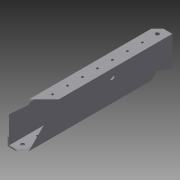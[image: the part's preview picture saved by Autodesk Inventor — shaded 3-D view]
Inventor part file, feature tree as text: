
AUTODESK INVENTOR PART (.ipt)
format: ipt  version: 2015 SP1 (Build 190203100, 203)  size: 138,752 bytes
history: native  units: in
note: dims shown in document units (in); Inventor stores cm internally (conversion verified against a paired STEP export)
features: sketch x4, projected_geometry x3, extrude x2, hole x2, pattern_linear x1
ambient origin geometry x8: Origin, YZ Plane, XZ Plane, XY Plane, X Axis, Y Axis, Z Axis, Center Point
bodies: Solid1 (feature_tree)
feature tree (12):
  extrude  "Extrusion1"  Depth=2.0in
  hole  "Hole1"  [1 undecoded]
  pattern_linear  "Rectangular Pattern1"  Spacing1=10.0in  [1 undecoded]
  extrude  "Extrusion2"  Depth=1.0in
  hole  "Hole2"  [1 undecoded]
  sketch  "Sketch1"  dims[d0=1.0in d1=2.0in]
  sketch  "Sketch2"  dims[d2=0.8in d3=1.8in]
  projected_geometry  "Projected Loop1"
  sketch  "Sketch3"  dims[d4=0.1in]
  projected_geometry  "Projected Loop2"
  sketch  "Sketch4"  dims[d5=0.1in d6=10.0in d7=0.0in d8=0.5in d9=0.5in d10=0.1562in d11=0.75in d12=0.375in d13=0.25in d14=0.5635in d15=1.0in d16=0.8108in d17=3.937in d19=1.0in d20=0.25in d21=0.25in d22=11.0in d23=0.0in d24=0.5in d25=6.5in d26=0.3125in d27=0.75in d28=0.375in d29=0.25in d30=0.5635in d31=1.0in d32=0.8108in]
  projected_geometry  "Projected Loop3"
note: 3 required parameter values undecoded (feature->parameter linkage not recoverable at this tier; creation-order binding heuristic only, values carry confidence <= 0.55)
